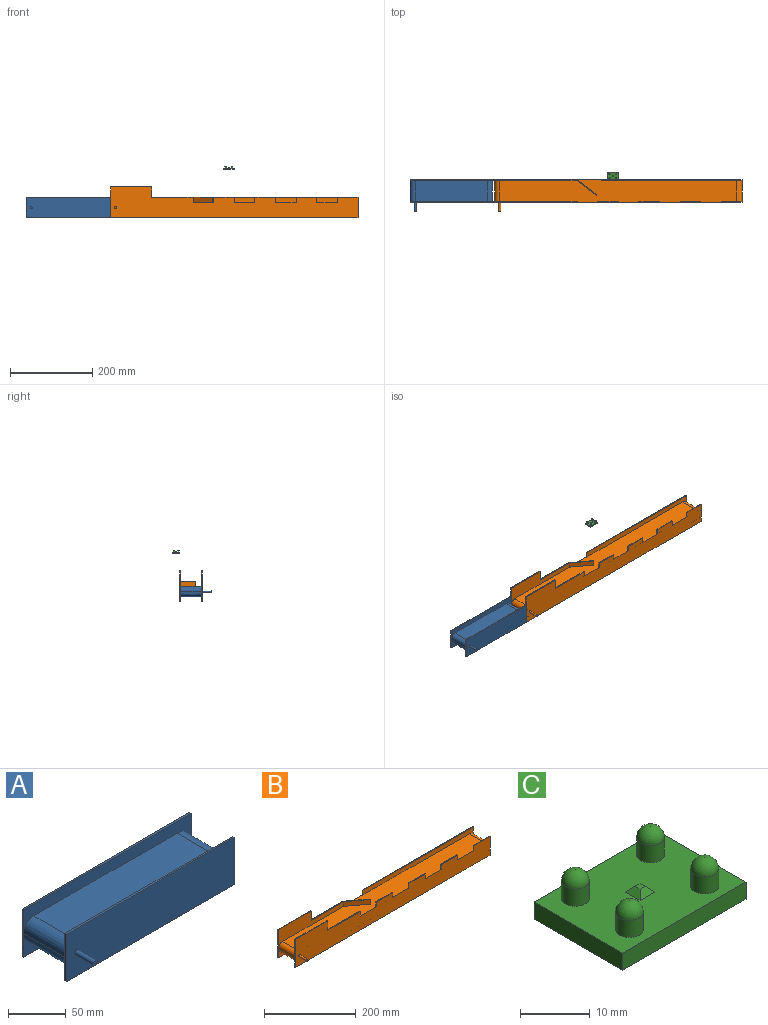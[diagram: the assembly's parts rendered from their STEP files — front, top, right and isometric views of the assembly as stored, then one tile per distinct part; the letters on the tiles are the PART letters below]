
ASSEMBLY  parts=3 mates=1
PART A: 20 faces, bbox 205.4x77.9x50.5 mm
  f0: plane 175x50mm, normal (0,0,1), area 8750mm2, adj f3,f5,f6,f11
  f1: plane 175x50mm, normal (0,0,-1), area 8750mm2, adj f2,f4,f6,f11
  f2: bspline ~55x12.5mm, area 1016.4mm2, adj f1,f3,f6,f11
  f3: bspline ~55x12.5mm, area 1016.4mm2, adj f0,f2,f6,f11
  f4: bspline ~55x12.5mm, area 1016.4mm2, adj f1,f5,f6,f11
  f5: bspline ~55x12.5mm, area 1016.4mm2, adj f0,f4,f6,f11
  f6: plane 205.44x50.46mm, normal (0,1,0), area 5360.9mm2, adj f0,f1,f2,f3,f4,f5,f7,f8
  f7: plane 50.02x2mm, normal (-1,0,0), area 100mm2, adj f6,f8,f9,f10
  f8: plane 205x2mm, normal (0,0,-1), area 410mm2, adj f6,f7,f10,f18
  f9: plane 205x2mm, normal (0,0,1), area 410mm2, adj f6,f7,f10,f18
  f10: plane 205x50.02mm, normal (0,-1,0), area 10234.1mm2, adj f7,f8,f9,f16,f18
  f11: plane 205.44x50.44mm, normal (0,-1,0), area 5357.1mm2, adj f0,f1,f2,f3,f4,f5,f12,f13
  f12: plane 205x2mm, normal (0,0,-1), area 410mm2, adj f11,f13,f15,f19
  f13: plane 50x2mm, normal (-1,0,0), area 100mm2, adj f11,f12,f14,f15
  f14: plane 205x2mm, normal (0,0,1), area 410mm2, adj f11,f13,f15,f19
  f15: plane 205x50mm, normal (0,1,0), area 10250mm2, adj f12,f13,f14,f19
  f16: cylinder r=2.5mm len=23mm, axis (0,1,0), area 361.3mm2, adj f10,f17
  f17: plane 5x5mm, normal (0,-1,0), area 19.6mm2, adj f16
  f18: plane 50.02x2mm, normal (1,0,0), area 100mm2, adj f6,f8,f9,f10
  f19: plane 50x2mm, normal (1,0,0), area 100mm2, adj f11,f12,f14,f15
PART B: 48 faces, bbox 600.4x77.9x75.4 mm
  f0: plane 100x2mm, normal (0,0,1), area 200mm2, adj f12,f27,f28,f44
  f1: plane 575x54mm, normal (0,0,1), area 29174mm2, adj f4,f6,f7,f8,f9,f11,f12,f17
  f2: plane 575x50mm, normal (0,0,-1), area 28750mm2, adj f3,f5,f10,f37
  f3: bspline ~55x12.5mm, area 1016.4mm2, adj f2,f4,f10,f37
  f4: bspline ~55x12.5mm, area 1016.4mm2, adj f1,f3,f11,f29
  f5: bspline ~55x12.5mm, area 1016.4mm2, adj f2,f6,f10,f37
  f6: bspline ~55x12.5mm, area 1016.4mm2, adj f1,f5,f28,f30
  f7: plane 50x12.5mm, normal (0,1,0), area 625mm2, adj f1,f24,f25,f26
  f8: plane 50x12.5mm, normal (0,1,0), area 625mm2, adj f1,f21,f22,f23
  f9: plane 50x12.52mm, normal (0,1,0), area 625.9mm2, adj f1,f18,f19,f20
  f10: plane 600.44x25.44mm, normal (0,1,0), area 7577mm2, adj f2,f3,f5,f13,f14,f15
  f11: plane 50.44x25.46mm, normal (0,1,0), area 650.5mm2, adj f1,f4,f15,f16,f17
  f12: plane 12.5x2mm, normal (1,0,0), area 25mm2, adj f0,f1,f27,f28
  f13: plane 75x2mm, normal (-1,0,0), area 150mm2, adj f10,f14,f27,f28,f45
  f14: plane 600x2mm, normal (0,0,-1), area 1200mm2, adj f10,f13,f15,f27
  f15: plane 50.02x2mm, normal (1,0,0), area 100mm2, adj f10,f11,f14,f16,f27
  f16: plane 50x2mm, normal (0,0,1), area 100mm2, adj f11,f15,f17,f27
  f17: plane 12.52x2mm, normal (-1,0,0), area 25mm2, adj f1,f11,f16,f27
  f18: plane 12.52x2mm, normal (1,0,0), area 25mm2, adj f1,f9,f19,f27
  f19: plane 50x2mm, normal (0,0,1), area 100mm2, adj f9,f18,f20,f27
  f20: plane 12.52x2mm, normal (-1,0,0), area 25mm2, adj f1,f9,f19,f27
  f21: plane 12.5x2mm, normal (1,0,0), area 25mm2, adj f1,f8,f22,f27
  f22: plane 50x2mm, normal (0,0,1), area 100mm2, adj f8,f21,f23,f27
  f23: plane 12.5x2mm, normal (-1,0,0), area 25mm2, adj f1,f8,f22,f27
  f24: plane 12.5x2mm, normal (1,0,0), area 25mm2, adj f1,f7,f25,f27
  f25: plane 50x2mm, normal (0,0,1), area 100mm2, adj f7,f24,f26,f27
  f26: plane 12.5x2mm, normal (-1,0,0), area 25mm2, adj f1,f7,f25,f27
  f27: plane 600x75mm, normal (0,-1,0), area 29982.2mm2, adj f0,f1,f12,f13,f14,f15,f16,f17
  f28: plane 200.44x50.44mm, normal (0,1,0), area 5025.5mm2, adj f0,f1,f6,f12,f13,f44,f45
  f29: plane 340.44x25.44mm, normal (0,-1,0), area 4275.5mm2, adj f1,f4,f31,f34,f35
  f30: plane 200.44x50.44mm, normal (0,-1,0), area 5022.5mm2, adj f1,f6,f32,f33,f39,f46,f47
  f31: plane 50x2mm, normal (1,0,0), area 100mm2, adj f29,f35,f36,f37,f38
  f32: plane 75x2mm, normal (-1,0,0), area 150mm2, adj f30,f36,f37,f38,f47
  f33: plane 148x38mm, normal (0,0,1), area 296mm2, adj f30,f36,f39,f40,f41,f46
  f34: plane 12.5x2mm, normal (-1,0,0), area 25mm2, adj f1,f29,f35,f36
  f35: plane 340x2mm, normal (0,0,1), area 680mm2, adj f29,f31,f34,f36
  f36: plane 600x75mm, normal (0,1,0), area 31750mm2, adj f1,f31,f32,f33,f34,f35,f38,f41
  f37: plane 600.44x25.44mm, normal (0,-1,0), area 7550.7mm2, adj f2,f3,f5,f31,f32,f38
  f38: plane 600x2mm, normal (0,0,-1), area 1200mm2, adj f31,f32,f36,f37
  f39: plane 48x36mm, normal (-0.6,-0.8,0), area 750mm2, adj f1,f30,f33,f40
  f40: plane 12.5x2mm, normal (1,0,0), area 25mm2, adj f1,f33,f39,f41
  f41: plane 48x36mm, normal (0.6,0.8,0), area 750mm2, adj f1,f33,f36,f40
  f42: cylinder r=2.5mm len=23mm, axis (0,1,0), area 361.3mm2, adj f27,f43
  f43: plane 5x5mm, normal (0,-1,0), area 19.6mm2, adj f42
  f44: plane 25x2mm, normal (1,0,0), area 50mm2, adj f0,f27,f28,f45
  f45: plane 100x2mm, normal (0,0,1), area 200mm2, adj f13,f27,f28,f44
  f46: plane 25x2mm, normal (1,0,0), area 50mm2, adj f30,f33,f36,f47
  f47: plane 100x2mm, normal (0,0,1), area 200mm2, adj f30,f32,f36,f46
PART C: 19 faces, bbox 25x18x8 mm
  f0: plane 25x3mm, normal (0,1,0), area 75mm2, adj f1,f3,f4,f5
  f1: plane 18x3mm, normal (-1,0,0), area 54mm2, adj f0,f2,f4,f5
  f2: plane 25x3mm, normal (0,-1,0), area 75mm2, adj f1,f3,f4,f5
  f3: plane 18x3mm, normal (1,0,0), area 54mm2, adj f0,f2,f4,f5
  f4: plane 25x18mm, normal (0,0,1), area 390.7mm2, adj f0,f1,f2,f3,f6,f7,f8,f9
  f5: plane 25x18mm, normal (0,0,-1), area 450mm2, adj f0,f1,f2,f3
  f6: cylinder r=2mm len=4mm, axis (0,0,-1), area 37.7mm2, adj f4,f11
  f7: cylinder r=2mm len=4mm, axis (0,0,-1), area 37.7mm2, adj f4,f10
  f8: cylinder r=2mm len=4mm, axis (0,0,-1), area 37.7mm2, adj f4,f12
  f9: cylinder r=2mm len=4mm, axis (0,0,-1), area 37.7mm2, adj f4,f13
  f10: sphere r=2mm, area 25.1mm2, adj f7
  f11: sphere r=2mm, area 25.1mm2, adj f6
  f12: sphere r=2mm, area 25.1mm2, adj f8
  f13: sphere r=2mm, area 25.1mm2, adj f9
  f14: plane 1x1mm, normal (0,0,1), area 1mm2, adj f15,f16,f17,f18
  f15: plane 3x1mm, normal (-0.71,0,0.71), area 2.8mm2, adj f4,f14,f16,f17
  f16: plane 3x1mm, normal (0,-0.71,0.71), area 2.8mm2, adj f4,f14,f15,f18
  f17: plane 3x1mm, normal (0,0.71,0.71), area 2.8mm2, adj f4,f14,f15,f18
  f18: plane 3x1mm, normal (0.71,0,0.71), area 2.8mm2, adj f4,f14,f16,f17
PLACE A t=(-585.47,-104.83,-29.3)mm
PLACE B t=(-380.47,-104.83,-29.3)mm
PLACE C t=(-115.62,-37.65,75.59)mm
MATE fastened A.f18 <-> B.f13  axis (1,0,0) through (-415.03,-109.36,-41.8)mm
